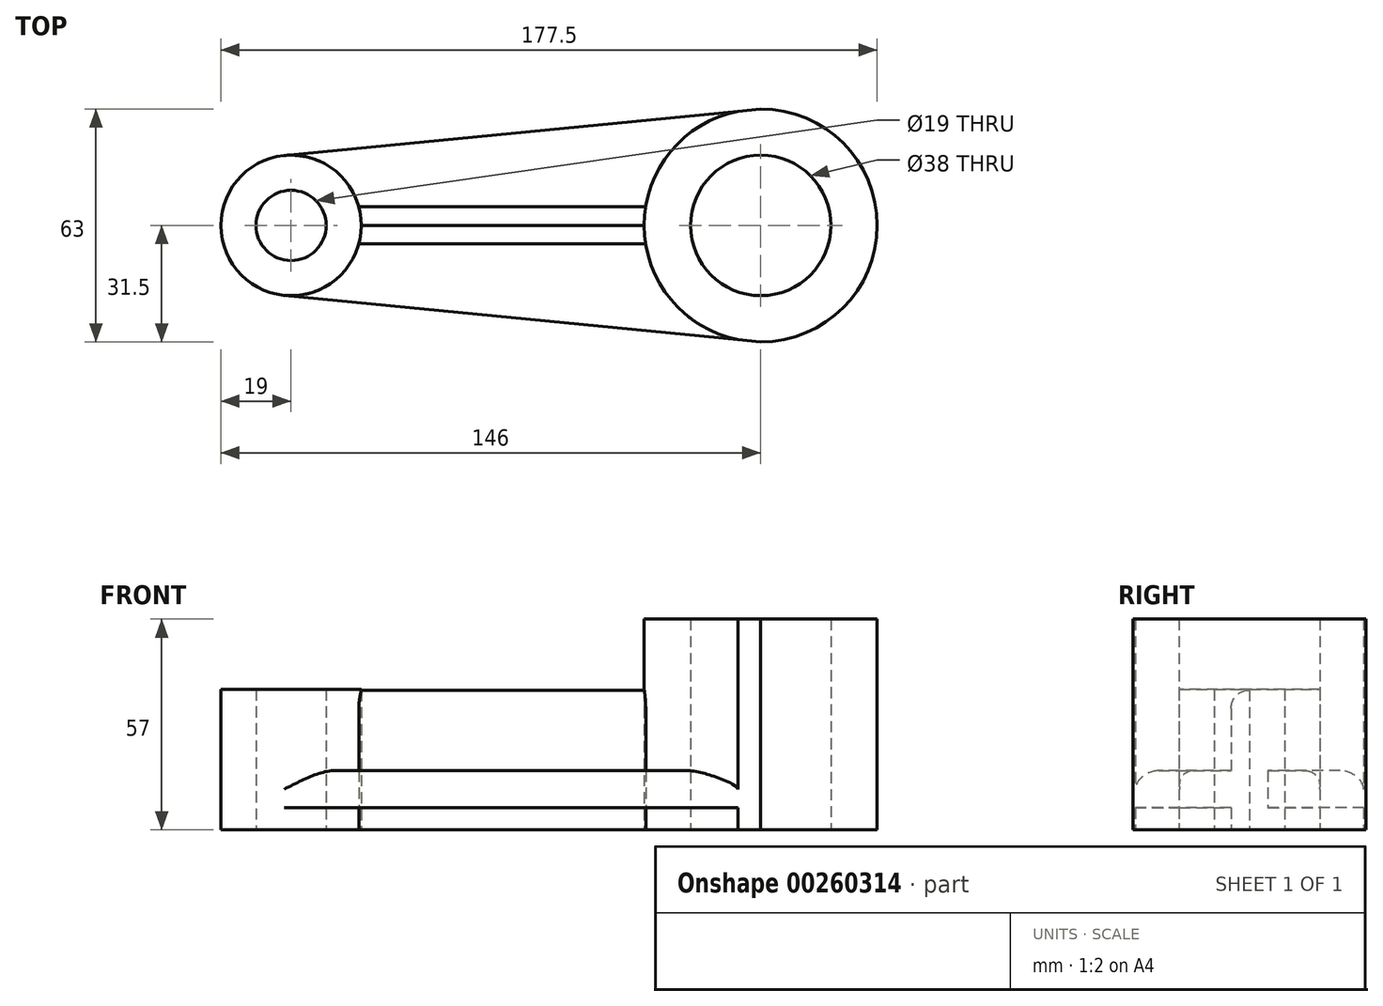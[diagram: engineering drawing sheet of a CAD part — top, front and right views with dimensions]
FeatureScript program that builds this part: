
annotation { "Feature Type Name" : "Feature", "Feature Type Description" : "" }
export const myFeature = defineFeature(function(context is Context, id is Id, definition is map)
    precondition{}
    {
        {
            var Q0;
            Q0=qCreatedBy(makeId("Top.planeOp"),FACE);
            var sketch = newSketch(context, id + "F0", { "sketchPlane" : qUnion([Q0])});
            skCircle(sketch, "E0", {"center": v(-127, 0) * mm, "radius": 19 * mm});
            skCircle(sketch, "E1", {"center": v(-127, 0) * mm, "radius": 9.5 * mm});
            skCircle(sketch, "E2", {"center": v(0, 0) * mm, "radius": 31.5 * mm});
            skCircle(sketch, "E3", {"center": v(0, 0) * mm, "radius": 19 * mm});
            skLineSegment(sketch, "E4", {"start": v(0, 31.5) * mm, "end": v(-128.85, 18.9) * mm});
            skLineSegment(sketch, "E5", {"start": v(0, -31.5) * mm, "end": v(-128.85, -18.9) * mm});
            skPoint(sketch, "E6.orphan", {"position": v(0, -31.5) * mm});
            skPoint(sketch, "E7.orphan", {"position": v(-127, -19.1) * mm});
            skPoint(sketch, "E8.orphan", {"position": v(0, 31.5) * mm});
            skLineSegment(sketch, "E9.bottom", {"start": v(-108.67, 5) * mm, "end": v(-30.98, 5) * mm});
            skLineSegment(sketch, "E9.top", {"start": v(-108.67, -5) * mm, "end": v(-31.1, -5) * mm});
            skLineSegment(sketch, "E9.left", {"start": v(-108.67, -5) * mm, "end": v(-108.67, -5) * mm});
            skLineSegment(sketch, "E10", {"start": v(-127, 0) * mm, "end": v(0, 0) * mm});
            skSolve(sketch);
        }
        {
            var Q0;
            Q0=makeQuery(id+"F0.imprint","IMPRINT",FACE,{"disambiguationData":[TD([[makeQuery(id+"F0.imprint","IMPRINT",EDGE,{"derivedFrom":sQuery(id+"F0.wireOp",EDGE,"E0")}),1.0]])]});
            extrude(context, id + "F1", {"entities" : qUnion([Q0]), "depth" : 38 * mm});
        }
        {
            var Q0;
            {var subQ5=sQuery(id+"F0.wireOp",EDGE,"E9.top");Q0=makeQuery(id+"F0.imprint","IMPRINT",FACE,{"disambiguationData":[TD([[makeQuery(id+"F0.imprint","IMPRINT",EDGE,{"derivedFrom":subQ5}),-1.0]])]});}
            var Q1;
            {var subQ0=sQuery(id+"F0.wireOp",EDGE,"E4");var subQ1=sQuery(id+"F0.wireOp",EDGE,"E0");var subQ2=makeQuery(id+"F0.imprint","INTERSECT",VERTEX,{"derivedFrom":[subQ1,subQ0]});Q1=makeQuery(id+"F0.imprint","IMPRINT",FACE,{"disambiguationData":[TD([[makeQuery(id+"F0.imprint","IMPRINT",EDGE,{"disambiguationData":[TD([[subQ2,1.0]])],"derivedFrom":subQ1}),-1.0]])]});}
            extrude(context, id + "F2", {"entities" : qUnion([Q0, Q1]), "operationType" : NewBodyOperationType.ADD, "depth" : 16 * mm});
        }
        {
            var Q0;
            Q0=makeQuery(id+"F0.imprint","IMPRINT",FACE,{"disambiguationData":[TD([[makeQuery(id+"F0.imprint","IMPRINT",EDGE,{"derivedFrom":sQuery(id+"F0.wireOp",EDGE,"E3")}),-1.0]])]});
            extrude(context, id + "F3", {"entities" : qUnion([Q0]), "operationType" : NewBodyOperationType.ADD, "depth" : 57 * mm});
        }
        {
            var Q0;
            {var subQ5=sQuery(id+"F0.wireOp",EDGE,"E9.top");Q0=makeQuery(id+"F0.imprint","IMPRINT",FACE,{"disambiguationData":[TD([[makeQuery(id+"F0.imprint","IMPRINT",EDGE,{"derivedFrom":subQ5}),-1.0]])]});}
            var Q1;
            {var subQ0=sQuery(id+"F0.wireOp",EDGE,"E9.top");Q1=makeQuery(id+"F0.imprint","IMPRINT",FACE,{"disambiguationData":[TD([[makeQuery(id+"F0.imprint","IMPRINT",EDGE,{"derivedFrom":subQ0}),1.0]])]});}
            var Q2;
            {var subQ0=sQuery(id+"F0.wireOp",EDGE,"E4");var subQ1=sQuery(id+"F0.wireOp",EDGE,"E0");var subQ2=makeQuery(id+"F0.imprint","INTERSECT",VERTEX,{"derivedFrom":[subQ1,subQ0]});Q2=makeQuery(id+"F0.imprint","IMPRINT",FACE,{"disambiguationData":[TD([[makeQuery(id+"F0.imprint","IMPRINT",EDGE,{"disambiguationData":[TD([[subQ2,1.0]])],"derivedFrom":subQ1}),-1.0]])]});}
            extrude(context, id + "F4", {"entities" : qUnion([Q0, Q1, Q2]), "operationType" : NewBodyOperationType.REMOVE, "depth" : 6 * mm});
        }
        {
            var Q0;
            {var subQ0=sQuery(id+"F0.wireOp",EDGE,"E9.top");Q0=makeQuery(id+"F0.imprint","IMPRINT",FACE,{"disambiguationData":[TD([[makeQuery(id+"F0.imprint","IMPRINT",EDGE,{"derivedFrom":subQ0}),1.0]])]});}
            extrude(context, id + "F5", {"entities" : qUnion([Q0]), "operationType" : NewBodyOperationType.ADD, "depth" : 37.8 * mm});
        }
        {
            var Q0;
            Q0=makeQuery(id+"F2.opExtrude","CAP_EDGE",EDGE,{"disambiguationData":[OSD([sQuery(id+"F0.wireOp",EDGE,"E5")])],"isStart":false});
            var Q1;
            Q1=makeQuery(id+"F4.boolean.opBoolean","COPY",EDGE,{"derivedFrom":makeQuery(id+"F4.opExtrude","CAP_EDGE",EDGE,{"disambiguationData":[OSD([sQuery(id+"F0.wireOp",EDGE,"E5")])],"isStart":false})});
            var Q2;
            Q2=makeQuery(id+"F5.opExtrude","CAP_EDGE",EDGE,{"disambiguationData":[OSD([sQuery(id+"F0.wireOp",EDGE,"E9.top")])],"isStart":false});
            var Q3;
            Q3=makeQuery(id+"F5.opExtrude","CAP_EDGE",EDGE,{"disambiguationData":[OSD([sQuery(id+"F0.wireOp",EDGE,"E9.bottom")])],"isStart":false});
            var Q4;
            Q4=makeQuery(id+"F4.boolean.opBoolean","COPY",EDGE,{"derivedFrom":makeQuery(id+"F4.opExtrude","CAP_EDGE",EDGE,{"disambiguationData":[OSD([sQuery(id+"F0.wireOp",EDGE,"E4")])],"isStart":false})});
            var Q5;
            Q5=makeQuery(id+"F2.opExtrude","CAP_EDGE",EDGE,{"disambiguationData":[OSD([sQuery(id+"F0.wireOp",EDGE,"E4")])],"isStart":false});
            fillet(context, id + "F6", {"entities" : qUnion([Q0, Q1, Q2, Q3, Q4, Q5]), "radius" : 5 * mm, "tangentPropagation" : true, "allowEdgeOverflow" : false});
        }
    });
